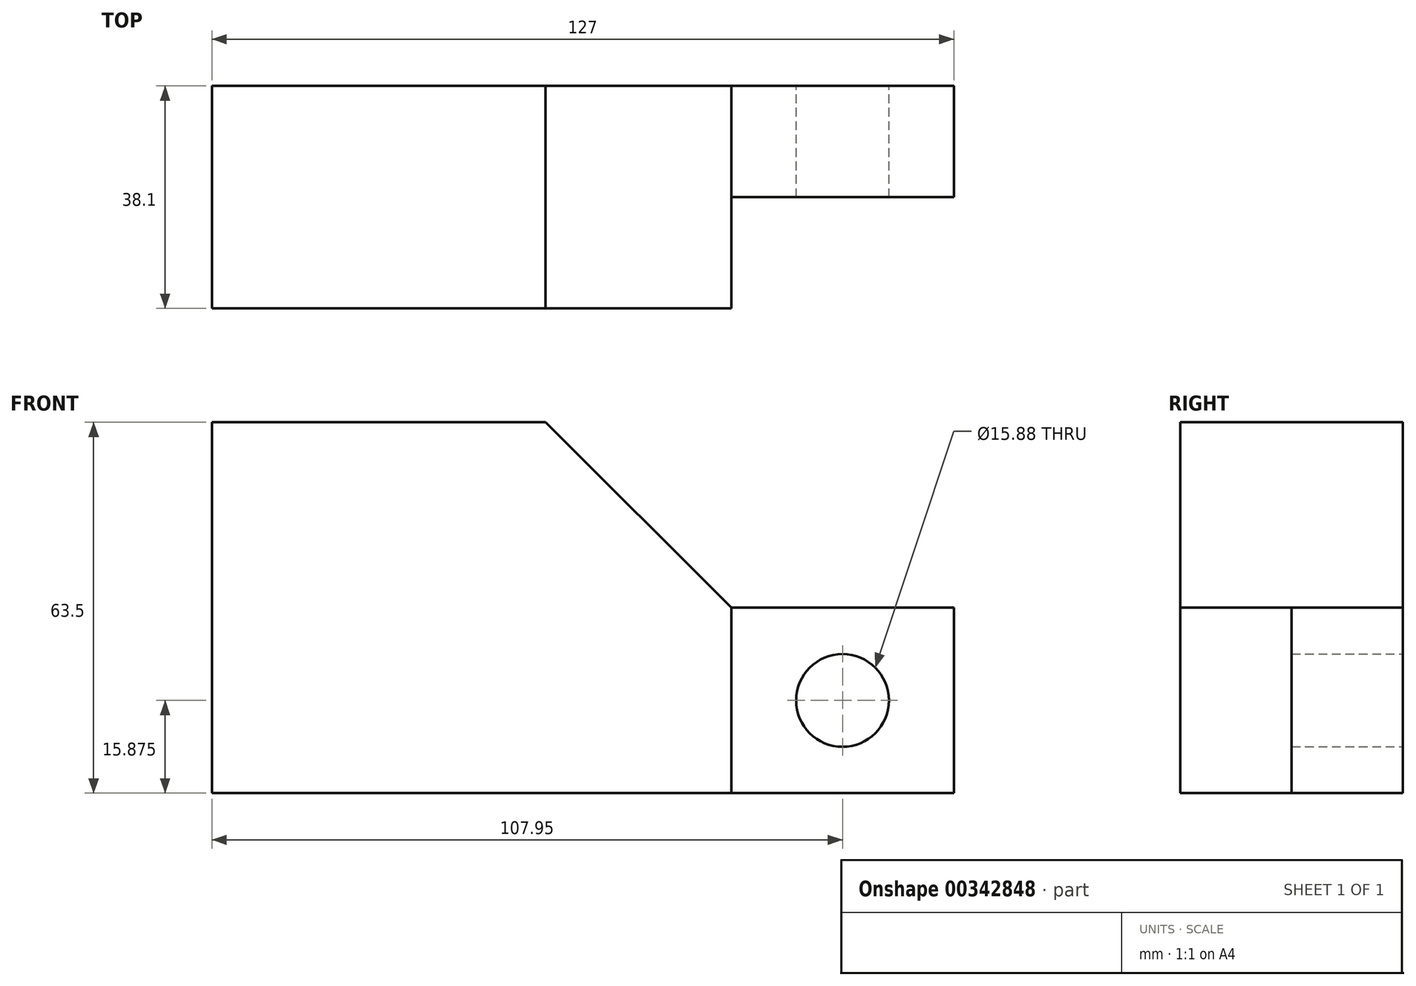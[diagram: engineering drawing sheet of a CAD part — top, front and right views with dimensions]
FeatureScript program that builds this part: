
annotation { "Feature Type Name" : "Feature", "Feature Type Description" : "" }
export const myFeature = defineFeature(function(context is Context, id is Id, definition is map)
    precondition{}
    {
        {
            var Q0;
            Q0=qCreatedBy(makeId("Front.planeOp"),FACE);
            var sketch = newSketch(context, id + "F0", { "sketchPlane" : qUnion([Q0])});
            skLineSegment(sketch, "E0.bottom", {"start": v(-63.5, -31.75) * mm, "end": v(63.5, -31.75) * mm});
            skLineSegment(sketch, "E0.top", {"start": v(-63.5, 31.75) * mm, "end": v(-6.35, 31.75) * mm});
            skLineSegment(sketch, "E0.left", {"start": v(-63.5, -31.75) * mm, "end": v(-63.5, 31.75) * mm});
            skLineSegment(sketch, "E0.right", {"start": v(63.5, -31.75) * mm, "end": v(63.5, 0) * mm});
            skPoint(sketch, "E0.middle", {"position": v(0, 0) * mm});
            skLineSegment(sketch, "E1", {"start": v(63.5, -31.75) * mm, "end": v(25.4, -31.75) * mm});
            skLineSegment(sketch, "E2", {"start": v(25.4, -31.75) * mm, "end": v(25.4, 0) * mm});
            skLineSegment(sketch, "E3", {"start": v(25.4, 0) * mm, "end": v(63.5, 0) * mm});
            skLineSegment(sketch, "E4", {"start": v(25.4, 0) * mm, "end": v(-6.35, 31.75) * mm});
            skPoint(sketch, "E5.orphan", {"position": v(63.5, 31.75) * mm});
            skLineSegment(sketch, "E6", {"start": v(63.5, 0) * mm, "end": v(63.5, -15.88) * mm});
            skLineSegment(sketch, "E7", {"start": v(63.5, 0) * mm, "end": v(44.45, 0) * mm});
            skCircle(sketch, "E8", {"center": v(44.45, -15.88) * mm, "radius": 7.94 * mm});
            skSolve(sketch);
        }
        {
            var Q0;
            Q0=makeQuery(id+"F0.imprint","IMPRINT",FACE,{"disambiguationData":[TD([[makeQuery(id+"F0.imprint","IMPRINT",EDGE,{"derivedFrom":sQuery(id+"F0.wireOp",EDGE,"E0.bottom")}),1.0]])]});
            extrude(context, id + "F1", {"entities" : qUnion([Q0]), "depth" : 38.1 * mm});
        }
        {
            var Q0;
            Q0 = qSketchRegion(id + "F0", true);
            extrude(context, id + "F2", {"entities" : qUnion([Q0]), "operationType" : NewBodyOperationType.ADD, "depth" : 19.05 * mm});
        }
    });
